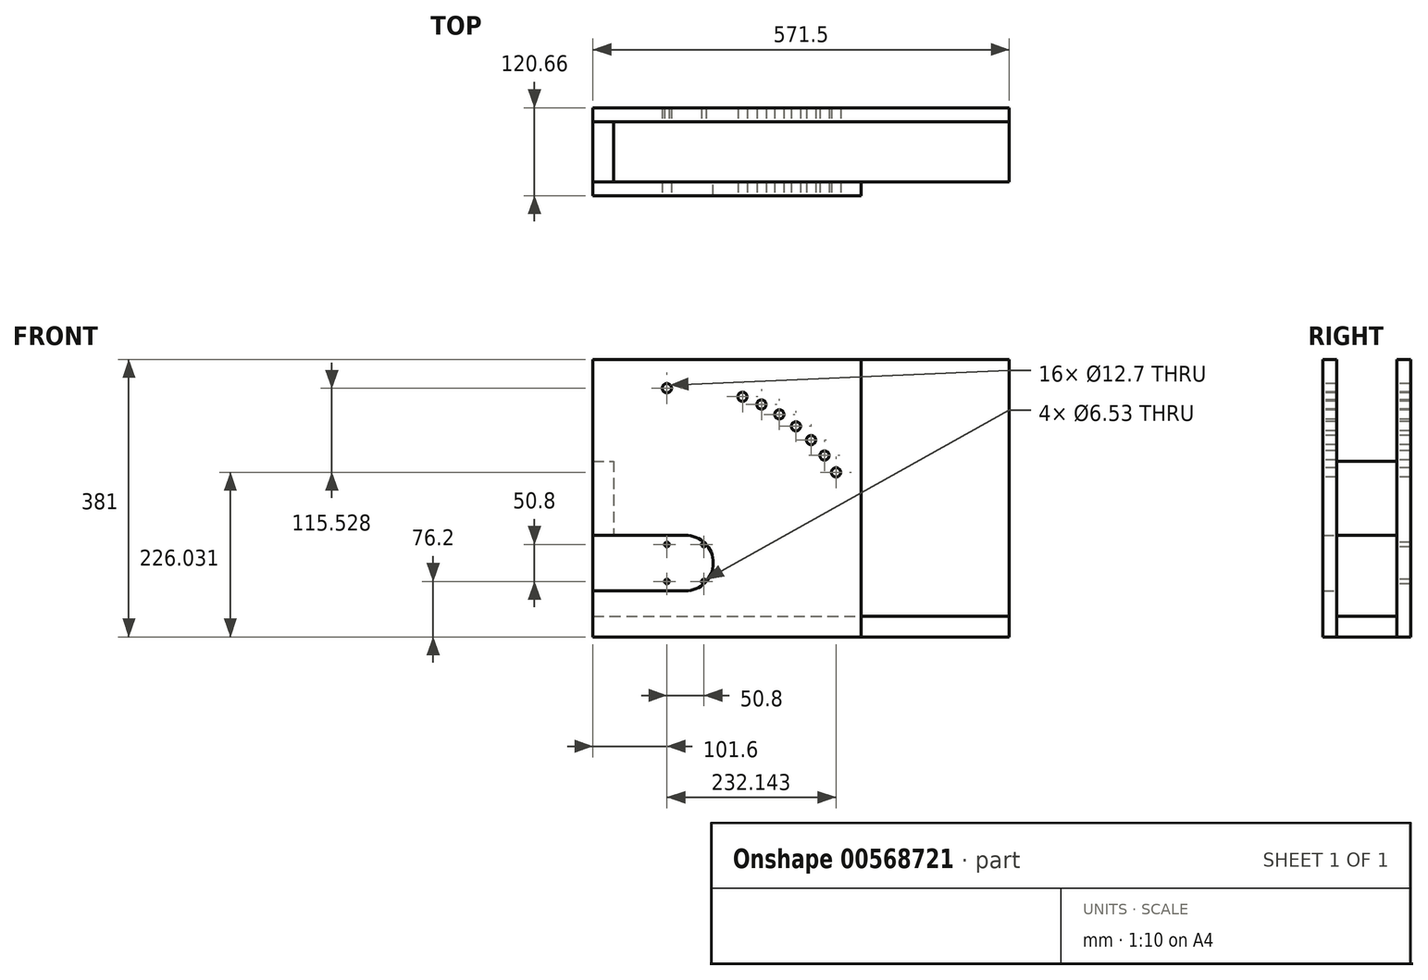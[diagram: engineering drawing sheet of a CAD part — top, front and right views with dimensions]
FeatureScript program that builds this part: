
annotation { "Feature Type Name" : "Feature", "Feature Type Description" : "" }
export const myFeature = defineFeature(function(context is Context, id is Id, definition is map)
    precondition{}
    {
        {
            var Q0;
            Q0=qCreatedBy(makeId("Top.planeOp"),FACE);
            var sketch = newSketch(context, id + "F0", { "sketchPlane" : qUnion([Q0])});
            skLineSegment(sketch, "E0.bottom", {"start": v(-127, 41.28) * mm, "end": v(444.5, 41.28) * mm});
            skLineSegment(sketch, "E0.top", {"start": v(-127, -41.27) * mm, "end": v(444.5, -41.27) * mm});
            skLineSegment(sketch, "E0.left", {"start": v(-127, 41.28) * mm, "end": v(-127, -41.28) * mm});
            skLineSegment(sketch, "E0.right", {"start": v(444.5, 41.27) * mm, "end": v(444.5, -41.27) * mm});
            skLineSegment(sketch, "E1", {"start": v(0, 41.27) * mm, "end": v(0, -41.27) * mm, "construction": true});
            skSolve(sketch);
        }
        {
            var Q0;
            Q0 = qSketchRegion(id + "F0", true);
            extrude(context, id + "F1", {"entities" : qUnion([Q0]), "depth" : 28.57 * mm, "offsetDistance" : 25.4 * mm});
        }
        {
            var Q0;
            Q0=makeQuery(id+"F1.opExtrude","SWEPT_FACE",FACE,{"disambiguationData":[OSD([sQuery(id+"F0.wireOp",EDGE,"E0.top")])]});
            var sketch = newSketch(context, id + "F2", { "sketchPlane" : qUnion([Q0])});
            skLineSegment(sketch, "E2.bottom", {"start": v(-127, 0) * mm, "end": v(241.3, 0) * mm});
            skLineSegment(sketch, "E2.top", {"start": v(-127, 381) * mm, "end": v(241.3, 381) * mm});
            skLineSegment(sketch, "E2.left", {"start": v(-127, 0) * mm, "end": v(-127, 63.5) * mm});
            skLineSegment(sketch, "E2.right", {"start": v(241.3, 0) * mm, "end": v(241.3, 381) * mm});
            skLineSegment(sketch, "E3", {"start": v(-127, 63.5) * mm, "end": v(0, 63.5) * mm});
            skArc(sketch, "E4", {"start": v(0, 63.5) * mm, "mid": v(38.1, 101.6) * mm, "end": v(0, 139.7) * mm});
            skLineSegment(sketch, "E5", {"start": v(0, 139.7) * mm, "end": v(-127, 139.7) * mm});
            skLineSegment(sketch, "E6.trimOffspring", {"start": v(-127, 139.7) * mm, "end": v(-127, 381) * mm});
            skSolve(sketch);
        }
        {
            var Q0;
            Q0 = qSketchRegion(id + "F2", true);
            extrude(context, id + "F3", {"entities" : qUnion([Q0]), "depth" : 19.05 * mm, "offsetDistance" : 25.4 * mm});
        }
        {
            var Q0;
            Q0=makeQuery(id+"F1.opExtrude","SWEPT_FACE",FACE,{"disambiguationData":[OSD([sQuery(id+"F0.wireOp",EDGE,"E0.bottom")])]});
            var sketch = newSketch(context, id + "F4", { "sketchPlane" : qUnion([Q0])});
            skLineSegment(sketch, "E7.bottom", {"start": v(127, 381) * mm, "end": v(-444.5, 381) * mm});
            skLineSegment(sketch, "E7.top", {"start": v(127, 0) * mm, "end": v(-444.5, 0) * mm});
            skLineSegment(sketch, "E7.left", {"start": v(127, 381) * mm, "end": v(127, 0) * mm});
            skLineSegment(sketch, "E7.right", {"start": v(-444.5, 381) * mm, "end": v(-444.5, 0) * mm});
            skSolve(sketch);
        }
        {
            var Q0;
            Q0 = qSketchRegion(id + "F4", true);
            extrude(context, id + "F5", {"entities" : qUnion([Q0]), "depth" : 19.05 * mm, "offsetDistance" : 25.4 * mm});
        }
        {
            var Q0;
            Q0=makeQuery(id+"F5.opExtrude","CAP_FACE",FACE,{"disambiguationData":[OSD([sQuery(id+"F4.wireOp",EDGE,"E7.bottom"),sQuery(id+"F4.wireOp",EDGE,"E7.top"),sQuery(id+"F4.wireOp",EDGE,"E7.left"),sQuery(id+"F4.wireOp",EDGE,"E7.right")])],"isStart":true});
            var sketch = newSketch(context, id + "F6", { "sketchPlane" : qUnion([Q0])});
            skLineSegment(sketch, "E8.bottom", {"start": v(38.1, 139.7) * mm, "end": v(-38.1, 139.7) * mm, "construction": true});
            skLineSegment(sketch, "E8.top", {"start": v(38.1, 63.5) * mm, "end": v(-38.1, 63.5) * mm, "construction": true});
            skLineSegment(sketch, "E8.left", {"start": v(38.1, 139.7) * mm, "end": v(38.1, 63.5) * mm, "construction": true});
            skLineSegment(sketch, "E8.right", {"start": v(-38.1, 139.7) * mm, "end": v(-38.1, 63.5) * mm, "construction": true});
            skPoint(sketch, "E8.middle", {"position": v(0, 101.6) * mm});
            skLineSegment(sketch, "E9.0", {"start": v(25.4, 127) * mm, "end": v(-25.4, 127) * mm, "construction": true});
            skLineSegment(sketch, "E9.1", {"start": v(25.4, 127) * mm, "end": v(25.4, 76.2) * mm, "construction": true});
            skLineSegment(sketch, "E9.2", {"start": v(25.4, 76.2) * mm, "end": v(-25.4, 76.2) * mm, "construction": true});
            skLineSegment(sketch, "E9.3", {"start": v(-25.4, 127) * mm, "end": v(-25.4, 76.2) * mm, "construction": true});
            skCircle(sketch, "E10", {"center": v(-25.4, 127) * mm, "radius": 3.26 * mm});
            skCircle(sketch, "E11", {"center": v(25.4, 127) * mm, "radius": 3.26 * mm});
            skCircle(sketch, "E12", {"center": v(-25.4, 76.2) * mm, "radius": 3.26 * mm});
            skCircle(sketch, "E13", {"center": v(25.4, 76.2) * mm, "radius": 3.26 * mm});
            skSolve(sketch);
        }
        {
            var Q0;
            Q0 = qSketchRegion(id + "F6", true);
            extrude(context, id + "F7", {"entities" : qUnion([Q0]), "operationType" : NewBodyOperationType.REMOVE, "oppositeDirection" : true, "depth" : 25.4 * mm, "offsetDistance" : 25.4 * mm});
        }
        {
            var Q0;
            Q0=makeQuery(id+"F5.opExtrude","CAP_FACE",FACE,{"disambiguationData":[OSD([sQuery(id+"F4.wireOp",EDGE,"E7.bottom"),sQuery(id+"F4.wireOp",EDGE,"E7.top"),sQuery(id+"F4.wireOp",EDGE,"E7.left"),sQuery(id+"F4.wireOp",EDGE,"E7.right")])],"isStart":true});
            var sketch = newSketch(context, id + "F8", { "sketchPlane" : qUnion([Q0])});
            skLineSegment(sketch, "E14", {"start": v(-127, 241.3) * mm, "end": v(-98.43, 241.3) * mm});
            skLineSegment(sketch, "E15", {"start": v(-98.43, 241.3) * mm, "end": v(-98.43, 139.7) * mm});
            skLineSegment(sketch, "E16", {"start": v(-98.43, 139.7) * mm, "end": v(-127, 139.7) * mm});
            skLineSegment(sketch, "E17", {"start": v(-127, 241.3) * mm, "end": v(-127, 139.7) * mm});
            skLineSegment(sketch, "E18", {"start": v(-98.43, 190.5) * mm, "end": v(0, 190.5) * mm, "construction": true});
            skSolve(sketch);
        }
        {
            var Q0;
            Q0 = qSketchRegion(id + "F8", true);
            var Q1;
            Q1=makeQuery(id+"F3.opExtrude","CAP_FACE",FACE,{"disambiguationData":[OSD([sQuery(id+"F2.wireOp",EDGE,"E2.bottom"),sQuery(id+"F2.wireOp",EDGE,"E2.top"),sQuery(id+"F2.wireOp",EDGE,"E2.left"),sQuery(id+"F2.wireOp",EDGE,"E2.right"),sQuery(id+"F2.wireOp",EDGE,"E3"),sQuery(id+"F2.wireOp",EDGE,"E4"),sQuery(id+"F2.wireOp",EDGE,"E5"),sQuery(id+"F2.wireOp",EDGE,"E6.trimOffspring")])],"isStart":true});
            var Q2;
            Q2=makeQuery(id+"F3.opExtrude","SWEPT_BODY",BODY,{"disambiguationData":[OSD([sQuery(id+"F2.wireOp",EDGE,"E2.bottom"),sQuery(id+"F2.wireOp",EDGE,"E2.top"),sQuery(id+"F2.wireOp",EDGE,"E2.left"),sQuery(id+"F2.wireOp",EDGE,"E2.right"),sQuery(id+"F2.wireOp",EDGE,"E3"),sQuery(id+"F2.wireOp",EDGE,"E4"),sQuery(id+"F2.wireOp",EDGE,"E5"),sQuery(id+"F2.wireOp",EDGE,"E6.trimOffspring")])]});
            extrude(context, id + "F9", {"entities" : qUnion([Q0]), "endBound" : BoundingType.UP_TO_SURFACE, "depth" : 25.4 * mm, "endBoundEntityFace" : qUnion([Q1]), "endBoundEntityBody" : qUnion([Q2]), "offsetDistance" : 25.4 * mm});
        }
        {
            var Q0;
            Q0=makeQuery(id+"F6.imprint","IMPRINT",FACE,{"disambiguationData":[TD([[makeQuery(id+"F6.imprint","IMPRINT",EDGE,{"derivedFrom":sQuery(id+"F6.wireOp",EDGE,"E10")}),-1.0]])]});
            var sketch = newSketch(context, id + "F10", { "sketchPlane" : qUnion([Q0])});
            skCircle(sketch, "E19", {"center": v(-95.25, 349.25) * mm, "radius": 6.35 * mm});
            skSolve(sketch);
        }
        {
            var Q0;
            Q0=makeQuery(id+"F3.opExtrude","CAP_FACE",FACE,{"disambiguationData":[OSD([sQuery(id+"F2.wireOp",EDGE,"E2.bottom"),sQuery(id+"F2.wireOp",EDGE,"E2.top"),sQuery(id+"F2.wireOp",EDGE,"E2.left"),sQuery(id+"F2.wireOp",EDGE,"E2.right"),sQuery(id+"F2.wireOp",EDGE,"E3"),sQuery(id+"F2.wireOp",EDGE,"E4"),sQuery(id+"F2.wireOp",EDGE,"E5"),sQuery(id+"F2.wireOp",EDGE,"E6.trimOffspring")])],"isStart":false});
            var sketch = newSketch(context, id + "F11", { "sketchPlane" : qUnion([Q0])});
            skLineSegment(sketch, "E20.bottom", {"start": v(-50.8, 120.65) * mm, "end": v(304.8, 120.65) * mm, "construction": true});
            skLineSegment(sketch, "E20.top", {"start": v(-50.8, 82.55) * mm, "end": v(304.8, 82.55) * mm, "construction": true});
            skLineSegment(sketch, "E20.left", {"start": v(-50.8, 120.65) * mm, "end": v(-50.8, 82.55) * mm, "construction": true});
            skLineSegment(sketch, "E20.right", {"start": v(304.8, 120.65) * mm, "end": v(304.8, 82.55) * mm, "construction": true});
            skLineSegment(sketch, "E21", {"start": v(0, 120.65) * mm, "end": v(0, 101.6) * mm, "construction": true});
            skLineSegment(sketch, "E22", {"start": v(0, 101.6) * mm, "end": v(425.25, 101.6) * mm, "construction": true});
            skCircle(sketch, "E23", {"center": v(0, 101.6) * mm, "radius": 247.65 * mm, "construction": true});
            skLineSegment(sketch, "E24", {"start": v(254, 127.18) * mm, "end": v(273.05, 127.18) * mm, "construction": true});
            skLineSegment(sketch, "E25", {"start": v(273.05, 127.18) * mm, "end": v(273.05, 165.1) * mm, "construction": true});
            skLineSegment(sketch, "E26", {"start": v(273.05, 165.1) * mm, "end": v(336.55, 165.1) * mm, "construction": true});
            skLineSegment(sketch, "E27", {"start": v(336.55, 165.1) * mm, "end": v(336.55, 127.18) * mm, "construction": true});
            skLineSegment(sketch, "E28", {"start": v(336.55, 127.18) * mm, "end": v(355.6, 127.18) * mm, "construction": true});
            skLineSegment(sketch, "E29", {"start": v(355.6, 127.18) * mm, "end": v(355.6, 120.65) * mm, "construction": true});
            skLineSegment(sketch, "E30", {"start": v(355.6, 120.65) * mm, "end": v(304.8, 120.65) * mm, "construction": true});
            skLineSegment(sketch, "E31", {"start": v(254, 127.18) * mm, "end": v(254, 120.65) * mm, "construction": true});
            skLineSegment(sketch, "E32", {"start": v(304.8, 165.1) * mm, "end": v(304.8, 120.65) * mm, "construction": true});
            skCircle(sketch, "E33", {"center": v(0, 101.6) * mm, "radius": 19.05 * mm, "construction": true});
            skLineSegment(sketch, "E34", {"start": v(-13.47, 115.07) * mm, "end": v(161.13, 289.67) * mm, "construction": true});
            skCircle(sketch, "E35", {"center": v(151.72, 289.24) * mm, "radius": 6.35 * mm});
            skCircle(sketch, "E36.0", {"center": v(0, 101.6) * mm, "radius": 241.3 * mm, "construction": true});
            skCircle(sketch, "E37.1.0", {"center": v(128.9, 305.58) * mm, "radius": 6.35 * mm});
            skLineSegment(sketch, "E37.1.1", {"start": v(-14.94, 113.42) * mm, "end": v(138.2, 307.1) * mm, "construction": true});
            skCircle(sketch, "E37.2.0", {"center": v(104.35, 319.17) * mm, "radius": 6.35 * mm});
            skLineSegment(sketch, "E37.2.1", {"start": v(-16.21, 111.6) * mm, "end": v(113.41, 321.76) * mm, "construction": true});
            skCircle(sketch, "E37.3.0", {"center": v(78.4, 329.81) * mm, "radius": 6.35 * mm});
            skLineSegment(sketch, "E37.3.1", {"start": v(-17.27, 109.65) * mm, "end": v(87.09, 333.43) * mm, "construction": true});
            skLineSegment(sketch, "E37.anchor1", {"start": v(0, 101.6) * mm, "end": v(151.72, 289.24) * mm, "construction": true});
            skLineSegment(sketch, "E37.anchor2", {"start": v(0, 101.6) * mm, "end": v(78.4, 329.81) * mm, "construction": true});
            skCircle(sketch, "E38.1.0", {"center": v(172.47, 270.36) * mm, "radius": 6.35 * mm});
            skLineSegment(sketch, "E38.1.1", {"start": v(-11.82, 116.54) * mm, "end": v(181.87, 269.69) * mm, "construction": true});
            skCircle(sketch, "E38.2.0", {"center": v(190.9, 249.2) * mm, "radius": 6.35 * mm});
            skLineSegment(sketch, "E38.2.1", {"start": v(-10, 117.81) * mm, "end": v(200.15, 247.44) * mm, "construction": true});
            skCircle(sketch, "E38.3.0", {"center": v(206.74, 226.03) * mm, "radius": 6.35 * mm});
            skLineSegment(sketch, "E38.3.1", {"start": v(-8.05, 118.87) * mm, "end": v(215.73, 223.22) * mm, "construction": true});
            skLineSegment(sketch, "E38.anchor2", {"start": v(0, 101.6) * mm, "end": v(206.74, 226.03) * mm, "construction": true});
            skLineSegment(sketch, "E39", {"start": v(-19.05, 101.6) * mm, "end": v(-19.05, 348.52) * mm, "construction": true});
            skCircle(sketch, "E40", {"center": v(-25.4, 341.56) * mm, "radius": 6.35 * mm});
            skSolve(sketch);
        }
        {
            var Q0;
            Q0 = qSketchRegion(id + "F11", true);
            extrude(context, id + "F12", {"entities" : qUnion([Q0]), "operationType" : NewBodyOperationType.REMOVE, "oppositeDirection" : true, "depth" : 25.4 * mm, "offsetDistance" : 25.4 * mm});
        }
        {
            var Q0;
            Q0=makeQuery(id+"F10.imprint","IMPRINT",FACE,{"disambiguationData":[TD([[makeQuery(id+"F10.imprint","IMPRINT",EDGE,{"derivedFrom":sQuery(id+"F10.wireOp",EDGE,"E19")}),-1.0]])]});
            var sketch = newSketch(context, id + "F13", { "sketchPlane" : qUnion([Q0])});
            skCircle(sketch, "E41.0", {"center": v(-25.4, 341.56) * mm, "radius": 6.35 * mm});
            skCircle(sketch, "E42.0", {"center": v(78.4, 329.81) * mm, "radius": 6.35 * mm});
            skCircle(sketch, "E42.1", {"center": v(104.35, 319.17) * mm, "radius": 6.35 * mm});
            skCircle(sketch, "E42.2", {"center": v(128.9, 305.58) * mm, "radius": 6.35 * mm});
            skCircle(sketch, "E42.3", {"center": v(151.72, 289.24) * mm, "radius": 6.35 * mm});
            skCircle(sketch, "E42.4", {"center": v(172.47, 270.36) * mm, "radius": 6.35 * mm});
            skCircle(sketch, "E42.5", {"center": v(190.9, 249.2) * mm, "radius": 6.35 * mm});
            skCircle(sketch, "E42.6", {"center": v(206.74, 226.03) * mm, "radius": 6.35 * mm});
            skSolve(sketch);
        }
        {
            var Q0;
            Q0 = qSketchRegion(id + "F13", true);
            extrude(context, id + "F14", {"entities" : qUnion([Q0]), "operationType" : NewBodyOperationType.REMOVE, "oppositeDirection" : true, "depth" : 25.4 * mm, "offsetDistance" : 25.4 * mm});
        }
    });
